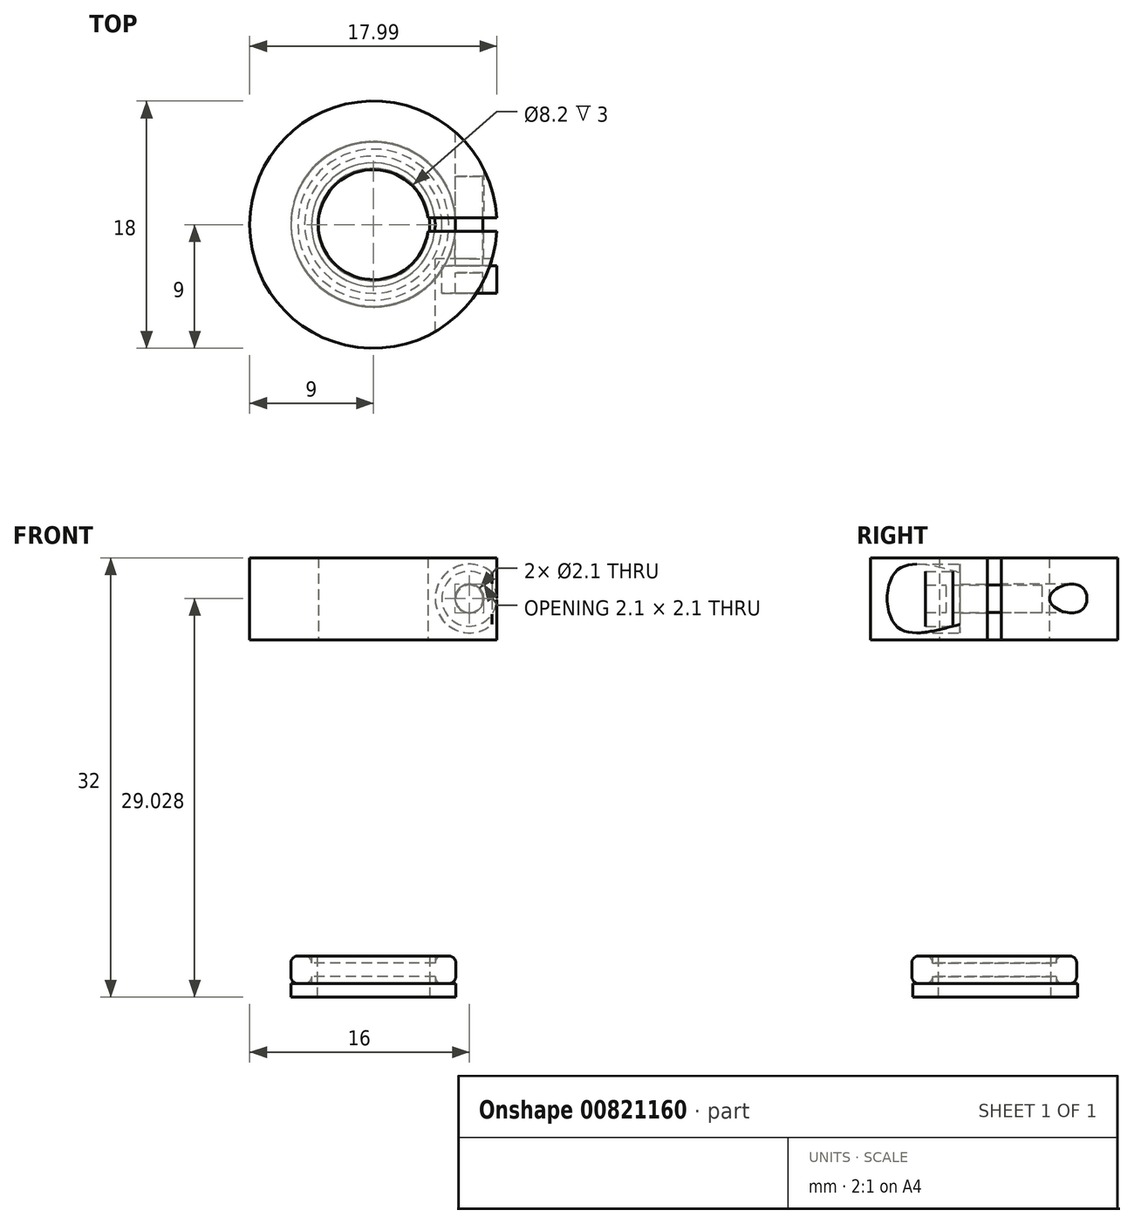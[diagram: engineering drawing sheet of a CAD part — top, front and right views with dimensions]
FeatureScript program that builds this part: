
annotation { "Feature Type Name" : "Feature", "Feature Type Description" : "" }
export const myFeature = defineFeature(function(context is Context, id is Id, definition is map)
    precondition{}
    {
        {
            var Q0;
            Q0=qCreatedBy(makeId("Top.planeOp"),FACE);
            var sketch = newSketch(context, id + "F0", { "sketchPlane" : qUnion([Q0])});
            skCircle(sketch, "E0", {"center": v(0, 0) * mm, "radius": 6 * mm});
            skCircle(sketch, "E1", {"center": v(0, 0) * mm, "radius": 4.5 * mm});
            skSolve(sketch);
        }
        {
            var Q0;
            Q0=makeQuery(id+"F0.imprint","IMPRINT",FACE,{"disambiguationData":[TD([[makeQuery(id+"F0.imprint","IMPRINT",EDGE,{"derivedFrom":sQuery(id+"F0.wireOp",EDGE,"E0")}),1.0]])]});
            extrude(context, id + "F1", {"entities" : qUnion([Q0]), "depth" : 2 * mm, "offsetDistance" : 25 * mm});
        }
        {
            var Q0;
            Q0=makeQuery(id+"F1.opExtrude","CAP_EDGE",EDGE,{"disambiguationData":[OSD([sQuery(id+"F0.wireOp",EDGE,"E0")])],"isStart":false});
            var Q1;
            Q1=makeQuery(id+"F1.opExtrude","CAP_EDGE",EDGE,{"disambiguationData":[OSD([sQuery(id+"F0.wireOp",EDGE,"E1")])],"isStart":false});
            var Q2;
            Q2=makeQuery(id+"F1.opExtrude","CAP_EDGE",EDGE,{"disambiguationData":[OSD([sQuery(id+"F0.wireOp",EDGE,"E0")])],"isStart":true});
            var Q3;
            Q3=makeQuery(id+"F1.opExtrude","CAP_EDGE",EDGE,{"disambiguationData":[OSD([sQuery(id+"F0.wireOp",EDGE,"E1")])],"isStart":true});
            fillet(context, id + "F2", {"entities" : qUnion([Q0, Q1, Q2, Q3]), "radius" : .5 * mm, "tangentPropagation" : true, "allowEdgeOverflow" : false});
        }
        {
            var Q0;
            Q0=qCreatedBy(makeId("Top.planeOp"),FACE);
            var sketch = newSketch(context, id + "F3", { "sketchPlane" : qUnion([Q0])});
            skCircle(sketch, "E2", {"center": v(0, 0) * mm, "radius": 4.1 * mm});
            skCircle(sketch, "E3", {"center": v(0, 0.06) * mm, "radius": 6 * mm});
            skCircle(sketch, "E4", {"center": v(0, 0) * mm, "radius": 4.5 * mm});
            skSolve(sketch);
        }
        {
            var Q0;
            Q0=makeQuery(id+"F3.imprint","IMPRINT",FACE,{"disambiguationData":[TD([[makeQuery(id+"F3.imprint","IMPRINT",EDGE,{"derivedFrom":sQuery(id+"F3.wireOp",EDGE,"E2")}),-1.0]])]});
            extrude(context, id + "F4", {"entities" : qUnion([Q0]), "depth" : 2 * mm, "offsetDistance" : 25 * mm});
        }
        {
            var Q0;
            Q0=makeQuery(id+"F3.imprint","IMPRINT",FACE,{"disambiguationData":[TD([[makeQuery(id+"F3.imprint","IMPRINT",EDGE,{"derivedFrom":sQuery(id+"F3.wireOp",EDGE,"E2")}),-1.0]])]});
            var Q1;
            Q1=makeQuery(id+"F3.imprint","IMPRINT",FACE,{"disambiguationData":[TD([[makeQuery(id+"F3.imprint","IMPRINT",EDGE,{"derivedFrom":sQuery(id+"F3.wireOp",EDGE,"E3")}),1.0]])]});
            extrude(context, id + "F5", {"entities" : qUnion([Q0, Q1]), "operationType" : NewBodyOperationType.ADD, "oppositeDirection" : true, "depth" : 1 * mm, "offsetDistance" : 25 * mm});
        }
        {
            var Q0;
            Q0=qCreatedBy(makeId("Top.planeOp"),FACE);
            cPlane(context, id + "F6", {"entities" : qUnion([Q0]), "cplaneType" : CPlaneType.OFFSET, "offset" : 25 * mm, "width" : 150 * mm, "height" : 150 * mm});
        }
        {
            var Q0;
            Q0=qCreatedBy(id+"F6.planeOp",FACE);
            var sketch = newSketch(context, id + "F7", { "sketchPlane" : qUnion([Q0])});
            skCircle(sketch, "E5", {"center": v(0, 0) * mm, "radius": 4 * mm});
            skCircle(sketch, "E6", {"center": v(0, 0) * mm, "radius": 9 * mm});
            skLineSegment(sketch, "E7", {"start": v(3.97, 0.5) * mm, "end": v(8.99, 0.5) * mm});
            skLineSegment(sketch, "E8.MirrorCS", {"start": v(3.97, -0.5) * mm, "end": v(8.99, -0.5) * mm});
            skSolve(sketch);
        }
        {
            var Q0;
            {var subQ0=sQuery(id+"F7.wireOp",EDGE,"E7");Q0=makeQuery(id+"F7.imprint","IMPRINT",FACE,{"disambiguationData":[TD([[makeQuery(id+"F7.imprint","IMPRINT",EDGE,{"derivedFrom":subQ0}),1.0]])]});}
            extrude(context, id + "F8", {"entities" : qUnion([Q0]), "depth" : 6 * mm, "offsetDistance" : 25 * mm});
        }
        {
            var Q0;
            Q0=qCreatedBy(makeId("Front.planeOp"),FACE);
            var sketch = newSketch(context, id + "F9", { "sketchPlane" : qUnion([Q0])});
            skCircle(sketch, "E9", {"center": v(7, 28.03) * mm, "radius": 2.5 * mm});
            skSolve(sketch);
        }
        {
            var Q0;
            Q0=sQuery(id+"F9.wireOp",VERTEX,"E9.center");
            var Q1;
            Q1=makeQuery(id+"F8.opExtrude","SWEPT_BODY",BODY,{"disambiguationData":[OSD([sQuery(id+"F7.wireOp",EDGE,"E5"),sQuery(id+"F7.wireOp",EDGE,"E6"),sQuery(id+"F7.wireOp",EDGE,"E7"),sQuery(id+"F7.wireOp",EDGE,"E8.MirrorCS")])]});
            hole(context, id + "F10", {"style" : HoleStyle.SIMPLE, "endStyle" : HoleEndStyle.THROUGH, "holeDiameter" : 2.1 * mm, "majorDiameter" : 5 * mm, "isTappedThrough" : true, "tappedDepth" : 6 * mm, "tapClearance" : 3, "startFromSketch" : true, "locations" : qUnion([Q0]), "scope" : qUnion([Q1])});
        }
        {
            var Q0;
            Q0=sQuery(id+"F9.wireOp",VERTEX,"E9.center");
            var Q1;
            Q1=makeQuery(id+"F8.opExtrude","SWEPT_BODY",BODY,{"disambiguationData":[OSD([sQuery(id+"F7.wireOp",EDGE,"E5"),sQuery(id+"F7.wireOp",EDGE,"E6"),sQuery(id+"F7.wireOp",EDGE,"E7"),sQuery(id+"F7.wireOp",EDGE,"E8.MirrorCS")])]});
            hole(context, id + "F11", {"style" : HoleStyle.SIMPLE, "endStyle" : HoleEndStyle.THROUGH, "oppositeDirection" : true, "holeDiameter" : 2.1 * mm, "majorDiameter" : 5 * mm, "isTappedThrough" : true, "tappedDepth" : 6 * mm, "tapClearance" : 3, "startFromSketch" : true, "locations" : qUnion([Q0]), "scope" : qUnion([Q1])});
        }
        {
            var Q0;
            Q0=makeQuery(id+"F9.imprint","IMPRINT",FACE,{"disambiguationData":[TD([[makeQuery(id+"F9.imprint","IMPRINT",EDGE,{"derivedFrom":sQuery(id+"F9.wireOp",EDGE,"E9")}),1.0]])]});
            var Q1;
            Q1=sQuery(id+"F9.wireOp",EDGE,"E9");
            extrude(context, id + "F12", {"entities" : qUnion([Q0]), "operationType" : NewBodyOperationType.REMOVE, "surfaceEntities" : qUnion([Q1]), "depth" : 10 * mm, "offsetDistance" : 25 * mm, "hasSecondDirection" : true, "secondDirectionOppositeDirection" : false, "secondDirectionDepth" : 2.5 * mm});
        }
        {
            var Q0;
            Q0=qCreatedBy(makeId("Front.planeOp"),FACE);
            var sketch = newSketch(context, id + "F13", { "sketchPlane" : qUnion([Q0])});
            skCircle(sketch, "E10", {"center": v(6.99, 28) * mm, "radius": 2 * mm});
            skCircle(sketch, "E11", {"center": v(6.99, 28) * mm, "radius": 1 * mm});
            skSolve(sketch);
        }
        {
            var Q0;
            Q0=makeQuery(id+"F13.imprint","IMPRINT",FACE,{"disambiguationData":[TD([[makeQuery(id+"F13.imprint","IMPRINT",EDGE,{"derivedFrom":sQuery(id+"F13.wireOp",EDGE,"E11")}),1.0]])]});
            extrude(context, id + "F14", {"entities" : qUnion([Q0]), "endBound" : BoundingType.SYMMETRIC, "depth" : 7 * mm, "offsetDistance" : 25 * mm});
        }
        {
            var Q0;
            Q0=makeQuery(id+"F13.imprint","IMPRINT",FACE,{"disambiguationData":[TD([[makeQuery(id+"F13.imprint","IMPRINT",EDGE,{"derivedFrom":sQuery(id+"F13.wireOp",EDGE,"E10")}),1.0]])]});
            extrude(context, id + "F15", {"entities" : qUnion([Q0]), "operationType" : NewBodyOperationType.ADD, "depth" : 5 * mm, "offsetDistance" : 25 * mm, "hasSecondDirection" : true, "secondDirectionOppositeDirection" : false, "secondDirectionDepth" : 3 * mm});
        }
    });
